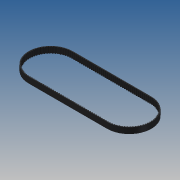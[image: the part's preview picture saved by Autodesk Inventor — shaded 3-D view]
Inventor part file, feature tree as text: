
AUTODESK INVENTOR PART (.ipt)
format: ipt  version: 2013 (Build 170138000, 138)  size: 427,008 bytes
history: native  units: mm
features: sketch x5, extrude x4, pattern_linear x1
ambient origin geometry x8: Origin, YZ Plane, XZ Plane, XY Plane, X Axis, Y Axis, Z Axis, Center Point
bodies: Solid1 (feature_tree)
feature tree (10):
  extrude  "Extrusion1"  Depth=22.281692mm
  extrude  "Extrusion2"  TaperAngle=180.0deg  [1 undecoded]
  extrude  "Extrusion4"  Depth=0.375mm
  sketch  "Sketch8"  dims[d15=6.0mm d16=0.0mm d17=6.0mm d18=0.0mm d19=1500.0mm]
  extrude  "Extrusion5"  Depth=0.629mm
  pattern_linear  "Rectangular Pattern1"  Spacing1=6.0mm  [1 undecoded]
  sketch  "Sketch1"  dims[d0=22.281692mm d2=22.281692mm]
  sketch  "Sketch2"  dims[d3=80.5mm d4=180.0deg]
  sketch  "Sketch5"  dims[d5=6.0mm d6=0.0mm d7=0.375mm]
  sketch  "Sketch7"  dims[d8=6.0mm d9=0.0mm d14=0.629mm]
note: 2 required parameter values undecoded (feature->parameter linkage not recoverable at this tier; creation-order binding heuristic only, values carry confidence <= 0.55)
